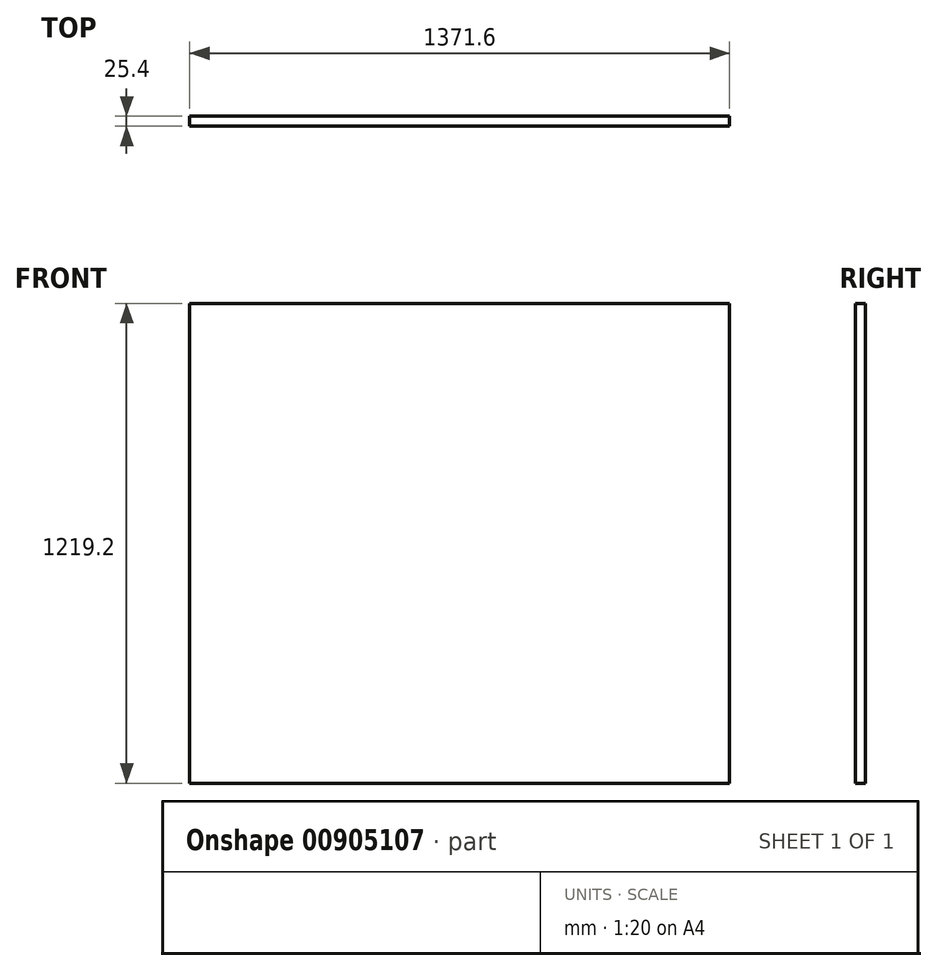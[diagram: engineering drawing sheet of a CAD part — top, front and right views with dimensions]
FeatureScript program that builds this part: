
annotation { "Feature Type Name" : "Feature", "Feature Type Description" : "" }
export const myFeature = defineFeature(function(context is Context, id is Id, definition is map)
    precondition{}
    {
        {
            var Q0;
            Q0=qCreatedBy(makeId("Front.planeOp"),FACE);
            var sketch = newSketch(context, id + "F0", { "sketchPlane" : qUnion([Q0])});
            skLineSegment(sketch, "E0.bottom", {"start": v(0, 0) * mm, "end": v(1371.6, 0) * mm});
            skLineSegment(sketch, "E0.top", {"start": v(0, 1219.2) * mm, "end": v(1371.6, 1219.2) * mm});
            skLineSegment(sketch, "E0.left", {"start": v(0, 0) * mm, "end": v(0, 1219.2) * mm});
            skLineSegment(sketch, "E0.right", {"start": v(1371.6, 0) * mm, "end": v(1371.6, 1219.2) * mm});
            skLineSegment(sketch, "E1.top", {"start": v(0, -50.8) * mm, "end": v(1371.6, -50.8) * mm});
            skLineSegment(sketch, "E1.left", {"start": v(0, 0) * mm, "end": v(0, -50.8) * mm});
            skLineSegment(sketch, "E1.right", {"start": v(1371.6, 0) * mm, "end": v(1371.6, -50.8) * mm});
            skLineSegment(sketch, "E2.top", {"start": v(0, -1066.8) * mm, "end": v(1371.6, -1066.8) * mm});
            skLineSegment(sketch, "E2.left", {"start": v(0, -50.8) * mm, "end": v(0, -1066.8) * mm});
            skLineSegment(sketch, "E2.right", {"start": v(1371.6, -50.8) * mm, "end": v(1371.6, -1066.8) * mm});
            skSolve(sketch);
        }
        {
            var Q0;
            Q0=makeQuery(id+"F0.imprint","IMPRINT",FACE,{"disambiguationData":[TD([[makeQuery(id+"F0.imprint","IMPRINT",EDGE,{"derivedFrom":sQuery(id+"F0.wireOp",EDGE,"E0.top")}),-1.0]])]});
            extrude(context, id + "F1", {"entities" : qUnion([Q0]), "depth" : 25.4 * mm, "offsetDistance" : 25.4 * mm});
        }
    });
